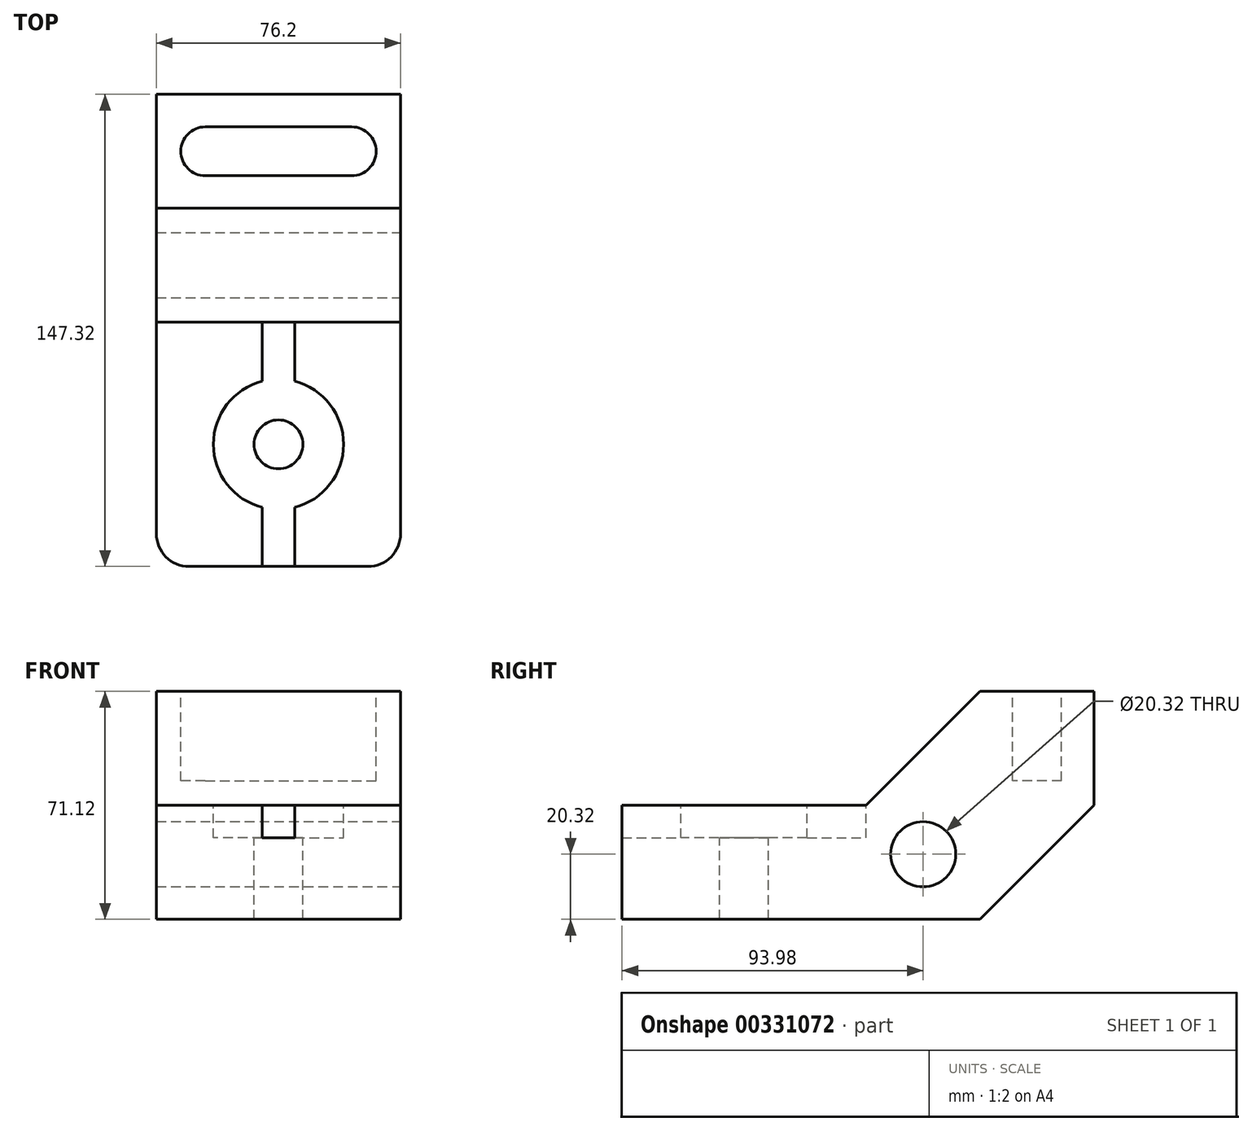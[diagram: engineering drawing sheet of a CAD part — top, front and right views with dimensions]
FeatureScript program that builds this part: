
annotation { "Feature Type Name" : "Feature", "Feature Type Description" : "" }
export const myFeature = defineFeature(function(context is Context, id is Id, definition is map)
    precondition{}
    {
        {
            var Q0;
            Q0=qCreatedBy(makeId("Right.planeOp"),FACE);
            var sketch = newSketch(context, id + "F0", { "sketchPlane" : qUnion([Q0])});
            skLineSegment(sketch, "E0", {"start": v(0, 0) * mm, "end": v(111.76, 0) * mm});
            skLineSegment(sketch, "E1", {"start": v(111.76, 0) * mm, "end": v(147.32, 35.56) * mm});
            skLineSegment(sketch, "E2", {"start": v(147.32, 35.56) * mm, "end": v(147.32, 71.12) * mm});
            skLineSegment(sketch, "E3", {"start": v(147.32, 71.12) * mm, "end": v(111.76, 71.12) * mm});
            skLineSegment(sketch, "E4", {"start": v(111.76, 71.12) * mm, "end": v(76.2, 35.56) * mm});
            skLineSegment(sketch, "E5", {"start": v(76.2, 35.56) * mm, "end": v(0, 35.56) * mm});
            skLineSegment(sketch, "E6", {"start": v(0, 35.56) * mm, "end": v(0, 0) * mm});
            skSolve(sketch);
        }
        {
            var Q0;
            Q0 = qSketchRegion(id + "F0", true);
            extrude(context, id + "F1", {"entities" : qUnion([Q0]), "depth" : 76.2 * mm});
        }
        {
            var Q0;
            Q0=makeQuery(id+"F1.opExtrude","CAP_FACE",FACE,{"disambiguationData":[OSD([sQuery(id+"F0.wireOp",EDGE,"E0"),sQuery(id+"F0.wireOp",EDGE,"E1"),sQuery(id+"F0.wireOp",EDGE,"E2"),sQuery(id+"F0.wireOp",EDGE,"E3"),sQuery(id+"F0.wireOp",EDGE,"E4"),sQuery(id+"F0.wireOp",EDGE,"E5"),sQuery(id+"F0.wireOp",EDGE,"E6")])],"isStart":false});
            var sketch = newSketch(context, id + "F2", { "sketchPlane" : qUnion([Q0])});
            skCircle(sketch, "E7", {"center": v(93.98, 20.32) * mm, "radius": 10.16 * mm});
            skSolve(sketch);
        }
        {
            var Q0;
            Q0=makeQuery(id+"F1.opExtrude","SWEPT_FACE",FACE,{"disambiguationData":[OSD([sQuery(id+"F0.wireOp",EDGE,"E3")])]});
            var sketch = newSketch(context, id + "F3", { "sketchPlane" : qUnion([Q0])});
            skArc(sketch, "E8", {"start": v(15.24, 137.16) * mm, "mid": v(7.62, 129.54) * mm, "end": v(15.24, 121.92) * mm});
            skArc(sketch, "E9", {"start": v(60.96, 121.92) * mm, "mid": v(68.58, 129.54) * mm, "end": v(60.96, 137.16) * mm});
            skLineSegment(sketch, "E10", {"start": v(15.24, 137.16) * mm, "end": v(60.96, 137.16) * mm});
            skLineSegment(sketch, "E11", {"start": v(15.24, 121.92) * mm, "end": v(60.96, 121.92) * mm});
            skSolve(sketch);
        }
        {
            var Q0;
            Q0=makeQuery(id+"F2.imprint","IMPRINT",FACE,{"disambiguationData":[TD([[makeQuery(id+"F2.imprint","IMPRINT",EDGE,{"derivedFrom":sQuery(id+"F2.wireOp",EDGE,"E7")}),1.0]])]});
            extrude(context, id + "F4", {"entities" : qUnion([Q0]), "operationType" : NewBodyOperationType.REMOVE, "endBound" : BoundingType.THROUGH_ALL, "oppositeDirection" : true, "depth" : 25.4 * mm});
        }
        {
            var Q0;
            Q0=makeQuery(id+"F1.opExtrude","SWEPT_FACE",FACE,{"disambiguationData":[OSD([sQuery(id+"F0.wireOp",EDGE,"E5")])]});
            var sketch = newSketch(context, id + "F5", { "sketchPlane" : qUnion([Q0])});
            skCircle(sketch, "E12", {"center": v(38.1, 38.1) * mm, "radius": 7.62 * mm});
            skSolve(sketch);
        }
        {
            var Q0;
            Q0=sQuery(id+"F5.wireOp",VERTEX,"E12.center");
            var Q1;
            Q1=makeQuery(id+"F1.opExtrude","SWEPT_BODY",BODY,{"disambiguationData":[OSD([sQuery(id+"F0.wireOp",EDGE,"E0"),sQuery(id+"F0.wireOp",EDGE,"E1"),sQuery(id+"F0.wireOp",EDGE,"E2"),sQuery(id+"F0.wireOp",EDGE,"E3"),sQuery(id+"F0.wireOp",EDGE,"E4"),sQuery(id+"F0.wireOp",EDGE,"E5"),sQuery(id+"F0.wireOp",EDGE,"E6")])]});
            hole(context, id + "F6", {"style" : HoleStyle.C_BORE, "endStyle" : HoleEndStyle.THROUGH, "holeDiameter" : 15.24 * mm, "cBoreDiameter" : 40.64 * mm, "cBoreDepth" : 10.16 * mm, "tappedDepth" : 12.7 * mm, "tapClearance" : 3, "locations" : qUnion([Q0]), "scope" : qUnion([Q1])});
        }
        {
            var Q0;
            Q0=makeQuery(id+"F1.opExtrude","SWEPT_FACE",FACE,{"disambiguationData":[OSD([sQuery(id+"F0.wireOp",EDGE,"E5")])]});
            var sketch = newSketch(context, id + "F7", { "sketchPlane" : qUnion([Q0])});
            skLineSegment(sketch, "E13.bottom", {"start": v(33.02, 0) * mm, "end": v(43.18, 0) * mm});
            skLineSegment(sketch, "E13.top", {"start": v(33.02, 76.2) * mm, "end": v(43.18, 76.2) * mm});
            skLineSegment(sketch, "E13.left", {"start": v(33.02, 0) * mm, "end": v(33.02, 76.2) * mm});
            skLineSegment(sketch, "E13.right", {"start": v(43.18, 0) * mm, "end": v(43.18, 76.2) * mm});
            skSolve(sketch);
        }
        {
            var Q0;
            {var subQ0=sQuery(id+"F7.wireOp",EDGE,"E13.top");Q0=makeQuery(id+"F7.imprint","IMPRINT",FACE,{"disambiguationData":[TD([[makeQuery(id+"F7.imprint","IMPRINT",EDGE,{"derivedFrom":subQ0}),1.0]])]});}
            var Q1;
            {var subQ0=sQuery(id+"F7.wireOp",EDGE,"E13.bottom");Q1=makeQuery(id+"F7.imprint","IMPRINT",FACE,{"disambiguationData":[TD([[makeQuery(id+"F7.imprint","IMPRINT",EDGE,{"derivedFrom":subQ0}),-1.0]])]});}
            extrude(context, id + "F8", {"entities" : qUnion([Q0, Q1]), "operationType" : NewBodyOperationType.REMOVE, "oppositeDirection" : true, "depth" : 10.16 * mm});
        }
        {
            var Q0;
            Q0=makeQuery(id+"F3.imprint","IMPRINT",FACE,{"disambiguationData":[TD([[makeQuery(id+"F3.imprint","IMPRINT",EDGE,{"derivedFrom":sQuery(id+"F3.wireOp",EDGE,"E8")}),1.0]])]});
            extrude(context, id + "F9", {"entities" : qUnion([Q0]), "operationType" : NewBodyOperationType.REMOVE, "oppositeDirection" : true, "depth" : 27.94 * mm});
        }
        {
            var Q0;
            Q0=makeQuery(id+"F1.opExtrude","CAP_EDGE",EDGE,{"disambiguationData":[OSD([sQuery(id+"F0.wireOp",EDGE,"E6")])],"isStart":false});
            var Q1;
            Q1=makeQuery(id+"F1.opExtrude","CAP_EDGE",EDGE,{"disambiguationData":[OSD([sQuery(id+"F0.wireOp",EDGE,"E6")])],"isStart":true});
            fillet(context, id + "F10", {"entities" : qUnion([Q0, Q1]), "radius" : 10.16 * mm, "tangentPropagation" : true, "allowEdgeOverflow" : false});
        }
    });
